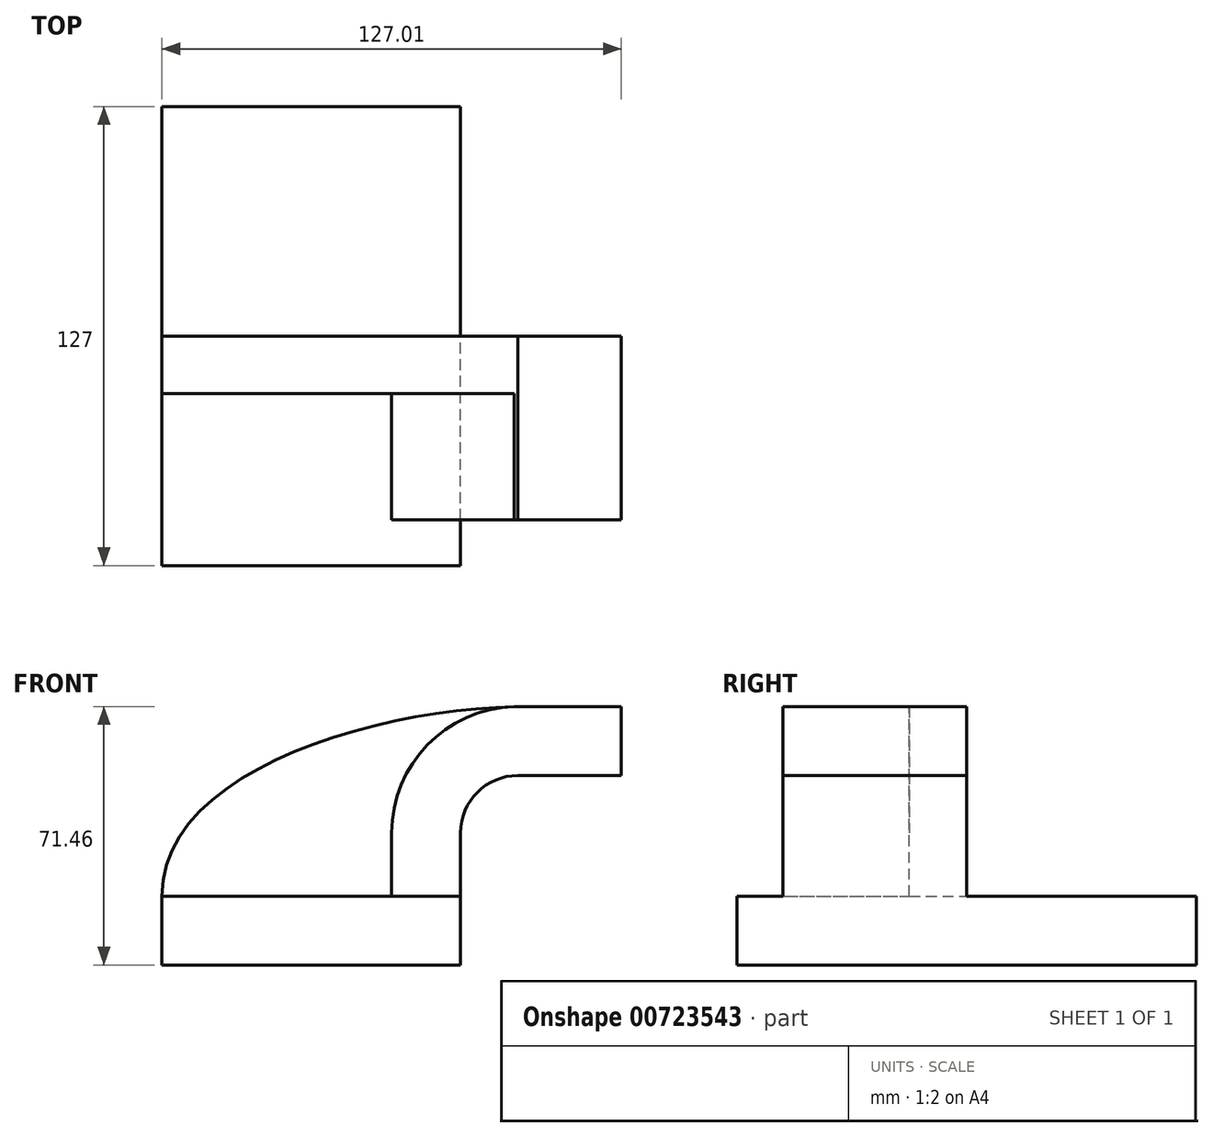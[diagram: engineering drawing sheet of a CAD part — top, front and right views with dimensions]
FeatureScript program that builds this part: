
annotation { "Feature Type Name" : "Feature", "Feature Type Description" : "" }
export const myFeature = defineFeature(function(context is Context, id is Id, definition is map)
    precondition{}
    {
        {
            var Q0;
            Q0=qCreatedBy(makeId("Front.planeOp"),FACE);
            var sketch = newSketch(context, id + "F0", { "sketchPlane" : qUnion([Q0])});
            skLineSegment(sketch, "E0.bottom", {"start": v(-41.28, -9.53) * mm, "end": v(41.28, -9.53) * mm});
            skLineSegment(sketch, "E0.top", {"start": v(-41.28, 9.52) * mm, "end": v(41.28, 9.52) * mm});
            skLineSegment(sketch, "E0.left", {"start": v(-41.27, -9.53) * mm, "end": v(-41.28, 9.52) * mm});
            skLineSegment(sketch, "E0.right", {"start": v(41.28, -9.53) * mm, "end": v(41.28, 9.52) * mm});
            skPoint(sketch, "E0.middle", {"position": v(0, 0) * mm});
            skLineSegment(sketch, "E1.bottom", {"start": v(60.33, 38.1) * mm, "end": v(111.12, 38.1) * mm});
            skLineSegment(sketch, "E1.top", {"start": v(60.33, 66.68) * mm, "end": v(111.12, 66.68) * mm});
            skLineSegment(sketch, "E1.left", {"start": v(60.33, 38.1) * mm, "end": v(60.33, 66.67) * mm});
            skLineSegment(sketch, "E1.right", {"start": v(111.12, 38.1) * mm, "end": v(111.12, 66.67) * mm});
            skPoint(sketch, "E1.middle", {"position": v(85.72, 52.39) * mm});
            skLineSegment(sketch, "E2", {"start": v(41.27, 9.52) * mm, "end": v(41.27, 27) * mm});
            skArc(sketch, "E3", {"start": v(41.27, 27) * mm, "mid": v(45.92, 38.23) * mm, "end": v(57.15, 42.88) * mm});
            skLineSegment(sketch, "E4.0", {"start": v(57.15, 61.93) * mm, "end": v(85.72, 61.93) * mm});
            skArc(sketch, "E4.1", {"start": v(22.22, 27) * mm, "mid": v(32.45, 51.7) * mm, "end": v(57.15, 61.93) * mm});
            skLineSegment(sketch, "E4.2", {"start": v(22.22, 9.52) * mm, "end": v(22.22, 27) * mm});
            skLineSegment(sketch, "E5", {"start": v(57.15, 42.88) * mm, "end": v(85.72, 42.88) * mm});
            skLineSegment(sketch, "E6", {"start": v(85.73, 38.1) * mm, "end": v(85.72, 66.68) * mm});
            skFitSpline(sketch, "E7", {"points": [v(-41.28, 9.53) * mm, v(57.15, 61.93) * mm], "startDerivative": vector(-1.07, 103.94) * mm, "endDerivative": vector(116.33, 1.25) * mm});
            skSolve(sketch);
        }
        {
            var Q0;
            Q0=makeQuery(id+"F0.imprint","IMPRINT",FACE,{"disambiguationData":[TD([[makeQuery(id+"F0.imprint","IMPRINT",EDGE,{"derivedFrom":sQuery(id+"F0.wireOp",EDGE,"E0.bottom")}),1.0]])]});
            extrude(context, id + "F1", {"entities" : qUnion([Q0]), "endBound" : BoundingType.SYMMETRIC, "depth" : 127 * mm, "offsetDistance" : 25.4 * mm});
        }
        {
            var Q0;
            {var subQ1=sQuery(id+"F0.wireOp",EDGE,"E2");Q0=makeQuery(id+"F0.imprint","IMPRINT",FACE,{"disambiguationData":[TD([[makeQuery(id+"F0.imprint","IMPRINT",EDGE,{"derivedFrom":subQ1}),1.0]])]});}
            var Q1;
            {var subQ0=sQuery(id+"F0.wireOp",EDGE,"E5");var subQ1=sQuery(id+"F0.wireOp",EDGE,"E1.left");var subQ2=makeQuery(id+"F0.imprint","INTERSECT",VERTEX,{"derivedFrom":[subQ1,subQ0]});Q1=makeQuery(id+"F0.imprint","IMPRINT",FACE,{"disambiguationData":[TD([[makeQuery(id+"F0.imprint","IMPRINT",EDGE,{"disambiguationData":[TD([[subQ2,-1.0]])],"derivedFrom":subQ1}),-1.0]])]});}
            extrude(context, id + "F2", {"entities" : qUnion([Q0, Q1]), "operationType" : NewBodyOperationType.ADD, "depth" : 50.8 * mm, "offsetDistance" : 25.4 * mm});
        }
        {
            var Q0;
            {var subQ3=sQuery(id+"F0.wireOp",EDGE,"E4.2");Q0=makeQuery(id+"F0.imprint","IMPRINT",FACE,{"disambiguationData":[TD([[makeQuery(id+"F0.imprint","IMPRINT",EDGE,{"derivedFrom":subQ3}),1.0]])]});}
            extrude(context, id + "F3", {"entities" : qUnion([Q0]), "operationType" : NewBodyOperationType.ADD, "depth" : 15.88 * mm, "offsetDistance" : 25.4 * mm});
        }
    });
